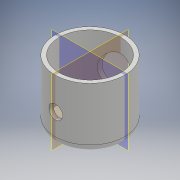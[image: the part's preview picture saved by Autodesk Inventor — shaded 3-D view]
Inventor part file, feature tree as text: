
AUTODESK INVENTOR PART (.ipt)
format: ipt  version: 2017 (Build 210142000, 142)  size: 148,480 bytes
history: native  units: mm
features: extrude x4, sketch x4, fillet x1
ambient origin geometry x8: Origin, YZ Plane, XZ Plane, XY Plane, X Axis, Y Axis, Z Axis, Center Point
bodies: Solid1 (feature_tree)
feature tree (9):
  extrude  "Extrusion1"  Depth=76.0mm
  extrude  "Extrusion2"  Depth=9.0mm
  fillet  "Fillet1"  Radius=17.0mm
  extrude  "Extrusion3"  Depth=35.5mm
  extrude  "Extrusion4"  Depth=35.5mm
  sketch  "Sketch1"  dims[d2=75.0mm d3=0.0mm d4=76.0mm]
  sketch  "Sketch2"  dims[d5=71.0mm d6=0.0mm d7=9.0mm d8=17.0mm]
  sketch  "Sketch3"  dims[d9=10.0mm d10=0.0mm d11=35.5mm]
  sketch  "Sketch6"  dims[d12=44.0mm d13=35.5mm d14=10.0mm d15=0.0mm]
